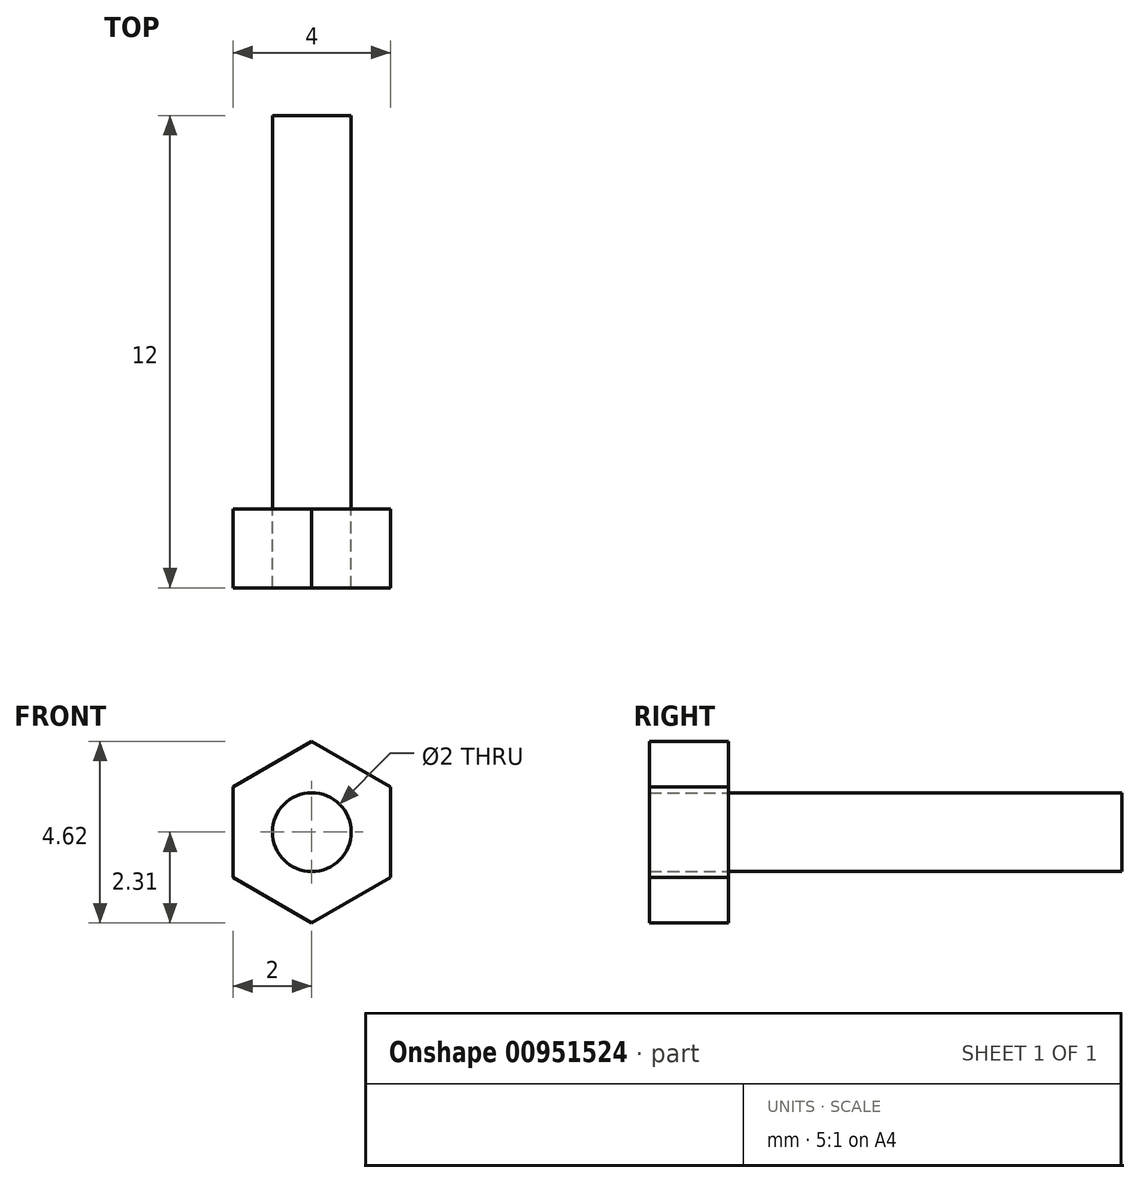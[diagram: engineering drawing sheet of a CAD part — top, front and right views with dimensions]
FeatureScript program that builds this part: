
annotation { "Feature Type Name" : "Feature", "Feature Type Description" : "" }
export const myFeature = defineFeature(function(context is Context, id is Id, definition is map)
    precondition{}
    {
        {
            var Q0;
            Q0=qCreatedBy(makeId("Front.planeOp"),FACE);
            var sketch = newSketch(context, id + "F0", { "sketchPlane" : qUnion([Q0])});
            skCircle(sketch, "E0", {"center": v(0, 0) * mm, "radius": 1 * mm});
            skCircle(sketch, "E1.cCircle", {"center": v(0, 0) * mm, "radius": 2 * mm, "construction": true});
            skLineSegment(sketch, "E1.0", {"start": v(-2, -1.15) * mm, "end": v(-2, 1.15) * mm});
            skLineSegment(sketch, "E1.1", {"start": v(-2, 1.15) * mm, "end": v(0, 2.3) * mm});
            skLineSegment(sketch, "E1.2", {"start": v(0, 2.3) * mm, "end": v(2, 1.15) * mm});
            skLineSegment(sketch, "E1.3", {"start": v(2, 1.15) * mm, "end": v(2, -1.15) * mm});
            skLineSegment(sketch, "E1.4", {"start": v(2, -1.15) * mm, "end": v(0, -2.3) * mm});
            skLineSegment(sketch, "E1.5", {"start": v(0, -2.3) * mm, "end": v(-2, -1.15) * mm});
            skPoint(sketch, "E1.0.midPoint", {"position": v(-2, 0) * mm});
            skSolve(sketch);
        }
        {
            var Q0;
            Q0=qSketchRegion(id+"F0",true);
            var Q1;
            Q1=makeQuery(id+"F0.imprint","IMPRINT",FACE,{"disambiguationData":[TD([[makeQuery(id+"F0.imprint","IMPRINT",EDGE,{"derivedFrom":sQuery(id+"F0.wireOp",EDGE,"E0")}),1.0]])]});
            extrude(context, id + "F1", {"entities" : qUnion([Q0, Q1]), "depth" : 2 * mm, "offsetDistance" : 25 * mm});
        }
        {
            var Q0;
            Q0=makeQuery(id+"F1.opExtrude","CAP_FACE",FACE,{"disambiguationData":[OSD([sQuery(id+"F0.wireOp",EDGE,"E1.0"),sQuery(id+"F0.wireOp",EDGE,"E1.1"),sQuery(id+"F0.wireOp",EDGE,"E1.2"),sQuery(id+"F0.wireOp",EDGE,"E1.3"),sQuery(id+"F0.wireOp",EDGE,"E1.4"),sQuery(id+"F0.wireOp",EDGE,"E1.5")])],"isStart":true});
            var sketch = newSketch(context, id + "F2", { "sketchPlane" : qUnion([Q0])});
            skCircle(sketch, "E2", {"center": v(0, 0) * mm, "radius": 1 * mm});
            skSolve(sketch);
        }
        {
            var Q0;
            Q0 = qSketchRegion(id + "F2", true);
            extrude(context, id + "F3", {"entities" : qUnion([Q0]), "operationType" : NewBodyOperationType.ADD, "depth" : 9 * mm, "offsetDistance" : 25 * mm});
        }
        {
            var Q0;
            Q0=qSketchRegion(id+"F2",true);
            extrude(context, id + "F4", {"entities" : qUnion([Q0]), "operationType" : NewBodyOperationType.ADD, "depth" : 10 * mm, "offsetDistance" : 25 * mm});
        }
        {
            var Q0;
            Q0=makeQuery(id+"F0.imprint","IMPRINT",FACE,{"disambiguationData":[TD([[makeQuery(id+"F0.imprint","IMPRINT",EDGE,{"derivedFrom":sQuery(id+"F0.wireOp",EDGE,"E0")}),-1.0]])]});
            extrude(context, id + "F5", {"entities" : qUnion([Q0]), "depth" : 2 * mm, "offsetDistance" : 25 * mm});
        }
    });
